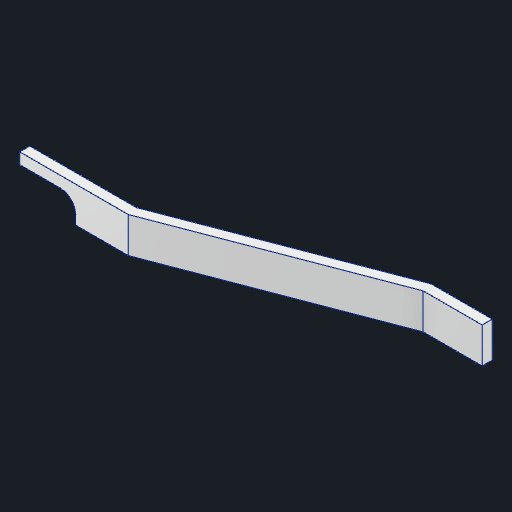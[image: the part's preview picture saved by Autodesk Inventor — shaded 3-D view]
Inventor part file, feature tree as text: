
AUTODESK INVENTOR PART (.ipt)
format: ipt  version: 2024 (Build 280153000, 153)  size: 95,744 bytes
history: native  units: in
note: dims shown in document units (in); Inventor stores cm internally (conversion verified against a paired STEP export)
features: other x3, sketch x2
ambient origin geometry x8: Origin, YZ Plane, XZ Plane, XY Plane, X Axis, Y Axis, Z Axis, Center Point
bodies: Solid1 (feature_tree)
feature tree (5):
  other  "Y_zigZag.ipt"
  other  "Solid1::Y_zigZag.ipt"
  other  "TaggingFeature1"
  sketch  "Sketch1"  dims[d0=0.3937in]
  sketch  "Sketch2"
